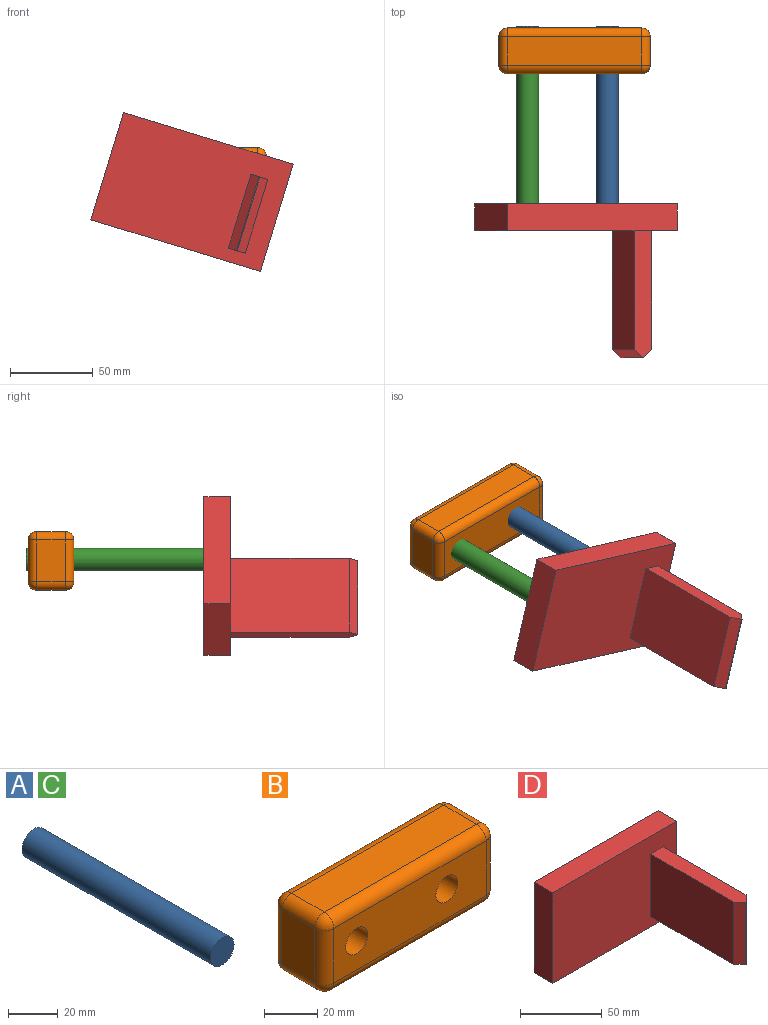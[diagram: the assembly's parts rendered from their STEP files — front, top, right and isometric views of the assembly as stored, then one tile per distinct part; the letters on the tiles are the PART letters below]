
ASSEMBLY  parts=4 mates=3
PART A: 3 faces, bbox 13.4x107.2x13.4 mm
  f0: cylinder r=6.68mm len=107.19mm, axis (0,1,0), area 4502.1mm2, adj f1,f2
  f1: plane 13.37x13.37mm, normal (0,-1,0), area 140.4mm2, adj f0
  f2: plane 13.37x13.37mm, normal (0,1,0), area 140.4mm2, adj f0
PART B: 28 faces, bbox 91.4x27.7x35.4 mm
  f0: plane 81.24x25.28mm, normal (0,1,0), area 1838.2mm2, adj f9,f10,f19,f20,f26,f27
  f1: plane 81.24x25.28mm, normal (0,-1,0), area 1838.2mm2, adj f12,f13,f21,f22,f26,f27
  f2: plane 81.24x17.53mm, normal (0,0,1), area 1423.8mm2, adj f11,f20,f21,f25
  f3: plane 25.28x17.53mm, normal (-1,0,0), area 443mm2, adj f14,f19,f22,f25
  f4: plane 81.24x17.53mm, normal (0,0,-1), area 1423.8mm2, adj f6,f9,f13,f14
  f5: plane 25.28x17.53mm, normal (1,0,0), area 443mm2, adj f6,f10,f11,f12
  f6: cylinder r=5.08mm len=17.53mm, axis (0,1,0), area 139.9mm2, adj f4,f5,f7,f8
  f7: sphere r=5.08mm, area 40.5mm2, adj f6,f9,f10
  f8: sphere r=5.08mm, area 40.5mm2, adj f6,f12,f13
  f9: cylinder r=5.08mm len=81.24mm, axis (-1,0,0), area 648.3mm2, adj f0,f4,f7,f15
  f10: cylinder r=5.08mm len=25.28mm, axis (0,0,-1), area 201.7mm2, adj f0,f5,f7,f16
  f11: cylinder r=5.08mm len=17.53mm, axis (0,-1,0), area 139.9mm2, adj f2,f5,f16,f17
  f12: cylinder r=5.08mm len=25.28mm, axis (0,0,1), area 201.7mm2, adj f1,f5,f8,f17
  f13: cylinder r=5.08mm len=81.24mm, axis (1,0,0), area 648.3mm2, adj f1,f4,f8,f18
  f14: cylinder r=5.08mm len=17.53mm, axis (0,-1,0), area 139.9mm2, adj f3,f4,f15,f18
  f15: sphere r=5.08mm, area 40.5mm2, adj f9,f14,f19
  f16: sphere r=5.08mm, area 40.5mm2, adj f10,f11,f20
  f17: sphere r=5.08mm, area 40.5mm2, adj f11,f12,f21
  f18: sphere r=5.08mm, area 40.5mm2, adj f13,f14,f22
  f19: cylinder r=5.08mm len=25.28mm, axis (0,0,1), area 201.7mm2, adj f0,f3,f15,f23
  f20: cylinder r=5.08mm len=81.24mm, axis (1,0,0), area 648.3mm2, adj f0,f2,f16,f23
  f21: cylinder r=5.08mm len=81.24mm, axis (-1,0,0), area 648.3mm2, adj f1,f2,f17,f24
  f22: cylinder r=5.08mm len=25.28mm, axis (0,0,-1), area 201.7mm2, adj f1,f3,f18,f24
  f23: sphere r=5.08mm, area 40.5mm2, adj f19,f20,f25
  f24: sphere r=5.08mm, area 40.5mm2, adj f21,f22,f25
  f25: cylinder r=5.08mm len=17.53mm, axis (0,1,0), area 139.9mm2, adj f2,f3,f23,f24
  f26: cylinder r=5.85mm len=27.69mm, axis (0,-1,0), area 1018mm2, adj f0,f1
  f27: cylinder r=5.85mm len=27.69mm, axis (0,-1,0), area 1018mm2, adj f0,f1
PART C: same geometry as A
PART D: 13 faces, bbox 107.1x93x67.8 mm
  f0: plane 107.15x67.78mm, normal (0,-1,0), area 6763.3mm2, adj f1,f2,f3,f4,f6,f7,f8,f9
  f1: plane 107.15x16.26mm, normal (0,0,1), area 1741.8mm2, adj f0,f2,f4,f5
  f2: plane 67.78x16.26mm, normal (-1,0,0), area 1101.8mm2, adj f0,f1,f3,f5
  f3: plane 107.15x16.26mm, normal (0,0,-1), area 1741.8mm2, adj f0,f2,f4,f5
  f4: plane 67.78x16.26mm, normal (1,0,0), area 1101.8mm2, adj f0,f1,f3,f5
  f5: plane 107.15x67.78mm, normal (0,1,0), area 7262.2mm2, adj f1,f2,f3,f4
  f6: plane 76.71x10.69mm, normal (0,0,1), area 794mm2, adj f0,f7,f9,f10,f11,f12
  f7: plane 71.63x46.68mm, normal (1,0,0), area 3343.9mm2, adj f0,f6,f8,f11
  f8: plane 76.71x10.69mm, normal (0,0,-1), area 794mm2, adj f0,f7,f9,f10,f11,f12
  f9: plane 71.63x46.68mm, normal (-1,0,0), area 3343.9mm2, adj f0,f6,f8,f12
  f10: plane 46.68x0.53mm, normal (0,-1,0), area 24.6mm2, adj f6,f8,f11,f12
  f11: plane 46.68x5.08mm, normal (0.71,-0.71,0), area 335.4mm2, adj f6,f7,f8,f10
  f12: plane 46.68x5.08mm, normal (-0.71,-0.71,0), area 335.4mm2, adj f6,f8,f9,f10
PLACE A rot(axis=(0,-1,0),73deg) t=(23.37,-21.66,53.93)mm
PLACE B rot(axis=(-0.52,-0.3,0.8),0deg) t=(-15.71,3.32,4.71)mm fixed
PLACE C rot(axis=(-0.52,-0.3,0.8),0deg) t=(11.71,-21.55,4.71)mm
PLACE D rot(axis=(0,1,0),17deg) t=(-10.73,-75.26,7.29)mm
MATE cylindrical A.f0 <-> B.f26  axis (0,1,0) through (8.34,-21.66,4.71)mm
MATE slider C.f0 <-> B.f27  axis (0,1,0) through (-39.75,-21.55,4.71)mm
MATE planar D.f5 <-> A.f0  axis (0,1,0) through (-0.56,-75.26,27.12)mm
